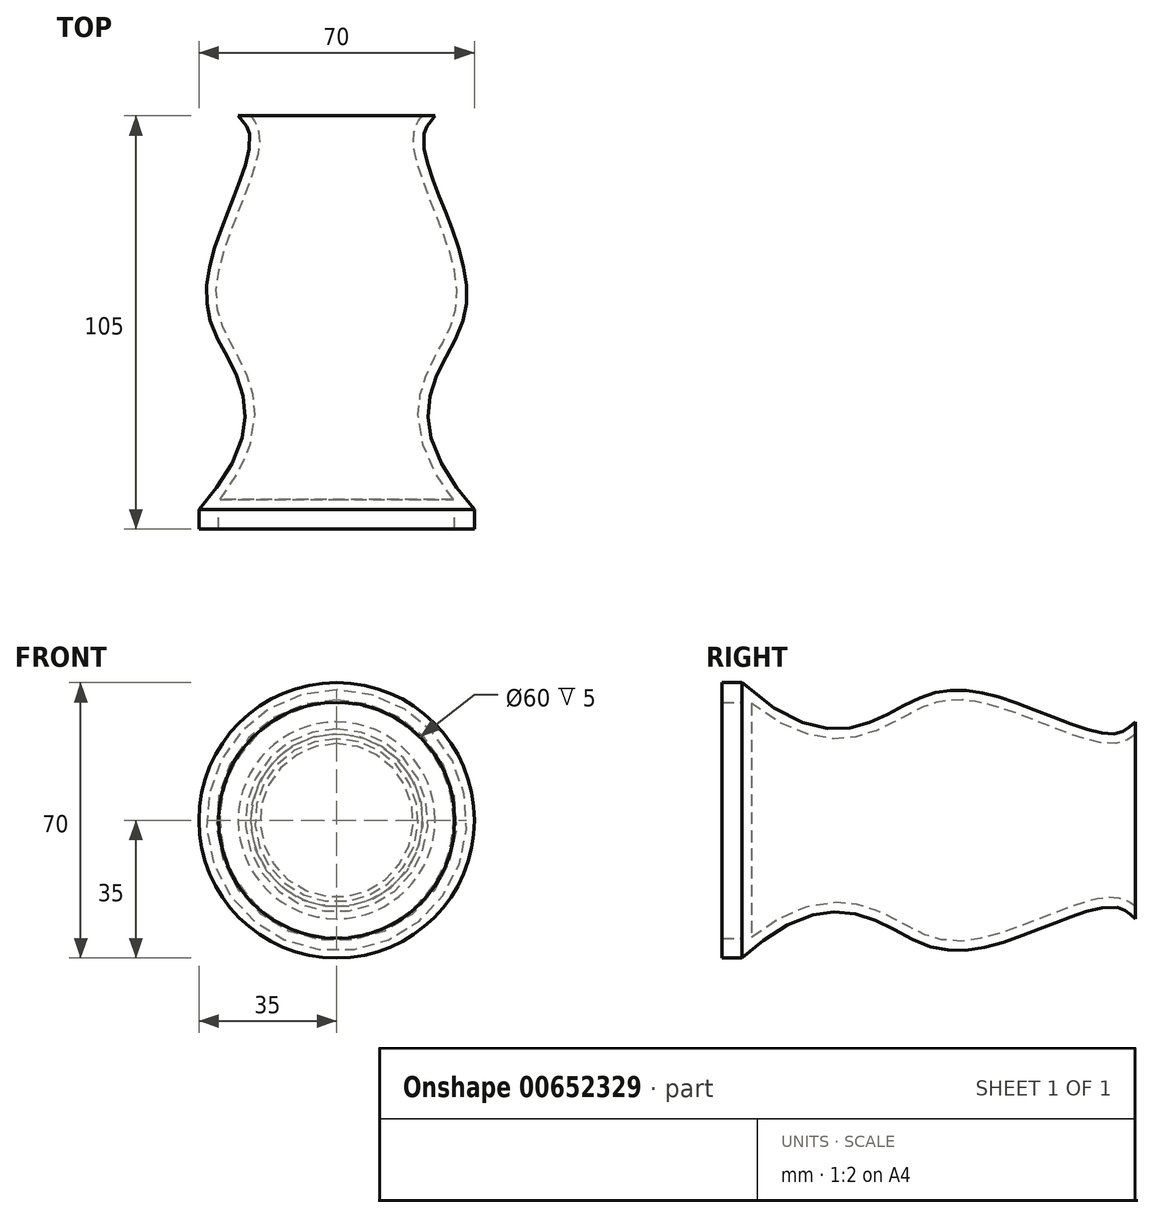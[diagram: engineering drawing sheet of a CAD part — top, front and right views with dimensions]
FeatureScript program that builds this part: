
annotation { "Feature Type Name" : "Feature", "Feature Type Description" : "" }
export const myFeature = defineFeature(function(context is Context, id is Id, definition is map)
    precondition{}
    {
        {
            var Q0;
            Q0=qCreatedBy(makeId("Top.planeOp"),FACE);
            var sketch = newSketch(context, id + "F0", { "sketchPlane" : qUnion([Q0])});
            skLineSegment(sketch, "E0", {"start": v(0, 79.94) * mm, "end": v(0, -20.06) * mm});
            skLineSegment(sketch, "E1", {"start": v(0, -20.06) * mm, "end": v(30, -20.06) * mm});
            skLineSegment(sketch, "E2", {"start": v(0, 79.94) * mm, "end": v(25, 79.94) * mm});
            skLineSegment(sketch, "E3", {"start": v(30, -20.06) * mm, "end": v(30, -25.06) * mm});
            skLineSegment(sketch, "E4", {"start": v(30, -25.06) * mm, "end": v(35, -25.06) * mm});
            skLineSegment(sketch, "E5", {"start": v(35, -25.06) * mm, "end": v(35, -20.06) * mm});
            skFitSpline(sketch, "E6", {"points": [v(25, 79.94) * mm, v(22.02, 74.68) * mm, v(30, 49.29) * mm, v(31.26, 25.44) * mm, v(35, -20.06) * mm], "startDerivative": vector(-25.49, -33.92) * mm, "endDerivative": vector(181.54, -201.98) * mm});
            skSolve(sketch);
        }
        {
            var Q0;
            Q0=makeQuery(id+"F0.imprint","IMPRINT",FACE,{"disambiguationData":[TD([[makeQuery(id+"F0.imprint","IMPRINT",EDGE,{"derivedFrom":sQuery(id+"F0.wireOp",EDGE,"E0")}),1.0]])]});
            var Q1;
            Q1=sQuery(id+"F0.wireOp",EDGE,"E0");
            revolve(context, id + "F1", {"surfaceOperationType" : NewSurfaceOperationType.NEW, "entities" : qUnion([Q0]), "axis" : qUnion([Q1]), "revolveType" : RevolveType.FULL});
        }
        {
            var Q0;
            Q0=makeQuery(id+"F1.opRevolve","SWEPT_FACE",FACE,{"disambiguationData":[OSD([sQuery(id+"F0.wireOp",EDGE,"E2")])]});
            shell(context, id + "F2", {"entities" : qUnion([Q0]), "thickness" : 2.5 * mm});
        }
    });
